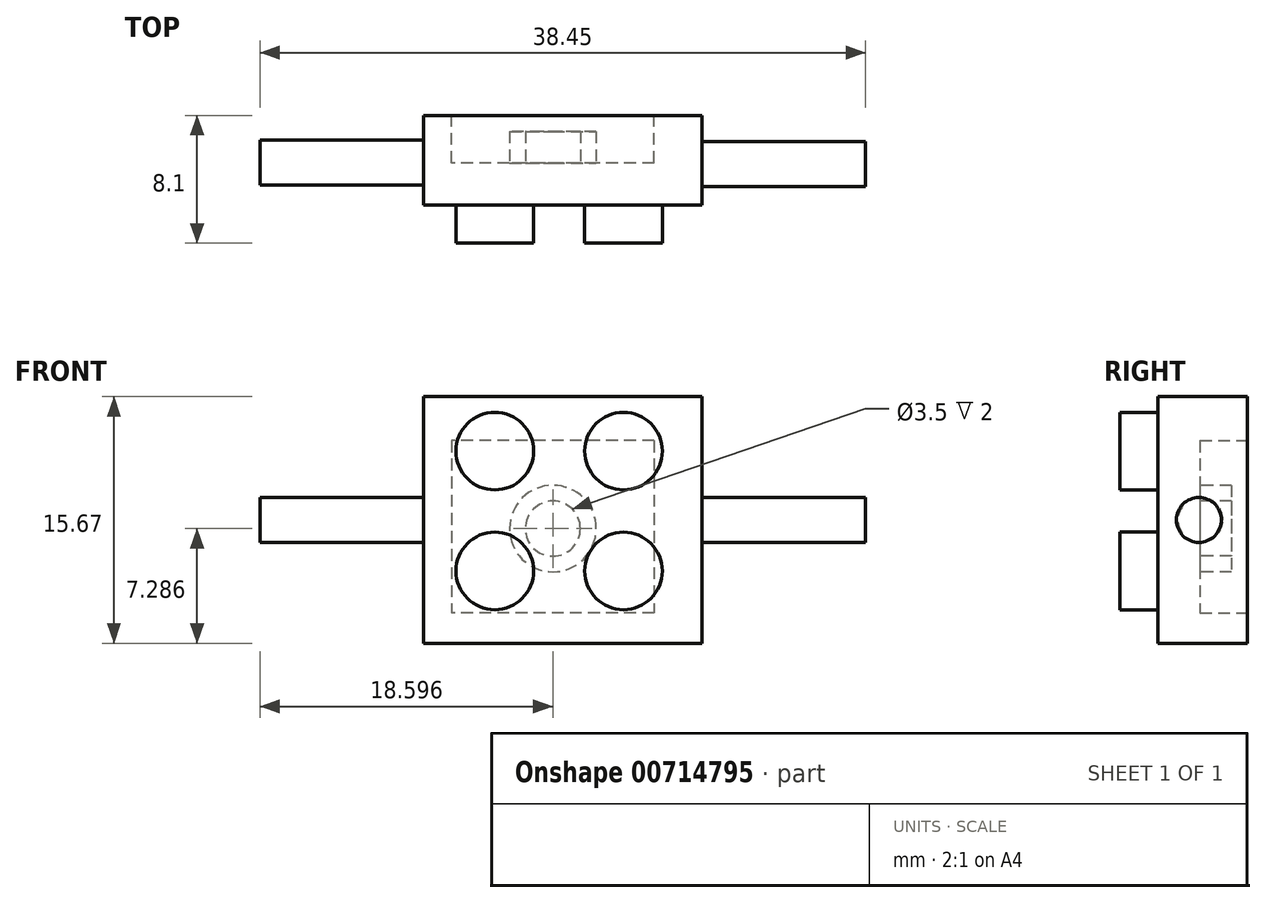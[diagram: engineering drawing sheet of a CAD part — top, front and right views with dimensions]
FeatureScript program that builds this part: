
annotation { "Feature Type Name" : "Feature", "Feature Type Description" : "" }
export const myFeature = defineFeature(function(context is Context, id is Id, definition is map)
    precondition{}
    {
        {
            var Q0;
            Q0=qCreatedBy(makeId("Front.planeOp"),FACE);
            var sketch = newSketch(context, id + "F0", { "sketchPlane" : qUnion([Q0])});
            skCircle(sketch, "E0", {"center": v(-31.02, 13.5) * mm, "radius": 7.84 * mm});
            skCircle(sketch, "E1", {"center": v(27.66, 13.5) * mm, "radius": 7.78 * mm});
            skCircle(sketch, "E2", {"center": v(-31.02, -35.79) * mm, "radius": 7.78 * mm});
            skCircle(sketch, "E3", {"center": v(27.66, -35.79) * mm, "radius": 7.78 * mm});
            skSolve(sketch);
        }
        {
            var Q0;
            Q0 = qSketchRegion(id + "F0", true);
            extrude(context, id + "F1", {"entities" : qUnion([Q0]), "depth" : 5.67 * mm, "offsetDistance" : 25 * mm});
        }
        {
            var Q0;
            Q0=qCreatedBy(makeId("Front.planeOp"),FACE);
            var sketch = newSketch(context, id + "F2", { "sketchPlane" : qUnion([Q0])});
            skLineSegment(sketch, "E4", {"start": v(-84.9, 44.94) * mm, "end": v(-67.21, 44.94) * mm});
            skLineSegment(sketch, "E5", {"start": v(-84.9, 29.27) * mm, "end": v(-67.21, 29.27) * mm});
            skPoint(sketch, "E6.start.orphan", {"position": v(-67.21, 39.5) * mm});
            skPoint(sketch, "E7.end.orphan", {"position": v(-84.9, 35.35) * mm});
            skLineSegment(sketch, "E8", {"start": v(-84.9, 44.94) * mm, "end": v(-84.9, 29.27) * mm});
            skLineSegment(sketch, "E9", {"start": v(-67.21, 44.94) * mm, "end": v(-67.21, 29.27) * mm});
            skSolve(sketch);
        }
        {
            var Q0;
            Q0 = qSketchRegion(id + "F2", true);
            extrude(context, id + "F3", {"entities" : qUnion([Q0]), "depth" : 5.67 * mm, "offsetDistance" : 25 * mm});
        }
        {
            var Q0;
            Q0=makeQuery(id+"F3.opExtrude","SWEPT_FACE",FACE,{"disambiguationData":[OSD([sQuery(id+"F2.wireOp",EDGE,"E8")])]});
            var sketch = newSketch(context, id + "F4", { "sketchPlane" : qUnion([Q0])});
            skPoint(sketch, "E10.centerSnap0", {"position": v(0, 37.1) * mm});
            skCircle(sketch, "E11", {"center": v(2.97, 37.1) * mm, "radius": 1.43 * mm});
            skSolve(sketch);
        }
        {
            var Q0;
            Q0 = qSketchRegion(id + "F4", true);
            extrude(context, id + "F5", {"entities" : qUnion([Q0]), "operationType" : NewBodyOperationType.ADD, "depth" : 10.38 * mm, "offsetDistance" : 25 * mm});
        }
        {
            var Q0;
            Q0=makeQuery(id+"F3.opExtrude","SWEPT_FACE",FACE,{"disambiguationData":[OSD([sQuery(id+"F2.wireOp",EDGE,"E9")])]});
            var sketch = newSketch(context, id + "F6", { "sketchPlane" : qUnion([Q0])});
            skCircle(sketch, "E12", {"center": v(-3.07, 37.1) * mm, "radius": 1.43 * mm});
            skPoint(sketch, "E12.centerSnap0", {"position": v(0, 37.1) * mm});
            skSolve(sketch);
        }
        {
            var Q0;
            Q0 = qSketchRegion(id + "F6", true);
            extrude(context, id + "F7", {"entities" : qUnion([Q0]), "operationType" : NewBodyOperationType.ADD, "depth" : 10.38 * mm, "offsetDistance" : 25 * mm});
        }
        {
            var Q0;
            Q0=makeQuery(id+"F3.opExtrude","CAP_FACE",FACE,{"disambiguationData":[OSD([sQuery(id+"F2.wireOp",EDGE,"E4"),sQuery(id+"F2.wireOp",EDGE,"E5"),sQuery(id+"F2.wireOp",EDGE,"E8"),sQuery(id+"F2.wireOp",EDGE,"E9")])],"isStart":false});
            var sketch = newSketch(context, id + "F8", { "sketchPlane" : qUnion([Q0])});
            skCircle(sketch, "E13", {"center": v(-80.37, 41.48) * mm, "radius": 2.46 * mm});
            skCircle(sketch, "E14", {"center": v(-72.2, 41.48) * mm, "radius": 2.46 * mm});
            skCircle(sketch, "E15", {"center": v(-72.2, 33.87) * mm, "radius": 2.46 * mm});
            skPoint(sketch, "E16.center.orphan", {"position": v(-80.37, 34.15) * mm});
            skCircle(sketch, "E17", {"center": v(-80.37, 33.87) * mm, "radius": 2.46 * mm});
            skSolve(sketch);
        }
        {
            var Q0;
            Q0 = qSketchRegion(id + "F8", true);
            extrude(context, id + "F9", {"entities" : qUnion([Q0]), "operationType" : NewBodyOperationType.ADD, "depth" : 2.42 * mm, "offsetDistance" : 25 * mm});
        }
        {
            var Q0;
            Q0=makeQuery(id+"F3.opExtrude","CAP_FACE",FACE,{"disambiguationData":[OSD([sQuery(id+"F2.wireOp",EDGE,"E4"),sQuery(id+"F2.wireOp",EDGE,"E5"),sQuery(id+"F2.wireOp",EDGE,"E8"),sQuery(id+"F2.wireOp",EDGE,"E9")])],"isStart":true});
            var sketch = newSketch(context, id + "F10", { "sketchPlane" : qUnion([Q0])});
            skLineSegment(sketch, "E18.bottom", {"start": v(70.25, 42.15) * mm, "end": v(83.12, 42.15) * mm});
            skLineSegment(sketch, "E18.top", {"start": v(70.25, 31.2) * mm, "end": v(83.12, 31.2) * mm});
            skLineSegment(sketch, "E18.left", {"start": v(70.25, 42.15) * mm, "end": v(70.25, 31.2) * mm});
            skLineSegment(sketch, "E18.right", {"start": v(83.12, 42.15) * mm, "end": v(83.12, 31.2) * mm});
            skSolve(sketch);
        }
        {
            var Q0;
            Q0 = qSketchRegion(id + "F10", true);
            extrude(context, id + "F11", {"entities" : qUnion([Q0]), "operationType" : NewBodyOperationType.REMOVE, "oppositeDirection" : true, "depth" : 3 * mm, "offsetDistance" : 25 * mm});
        }
        {
            var Q0;
            Q0=makeQuery(id+"F11.boolean.opBoolean","COPY",FACE,{"derivedFrom":makeQuery(id+"F11.opExtrude","CAP_FACE",FACE,{"disambiguationData":[OSD([sQuery(id+"F10.wireOp",EDGE,"E18.bottom"),sQuery(id+"F10.wireOp",EDGE,"E18.top"),sQuery(id+"F10.wireOp",EDGE,"E18.left"),sQuery(id+"F10.wireOp",EDGE,"E18.right")])],"isStart":false})});
            var sketch = newSketch(context, id + "F12", { "sketchPlane" : qUnion([Q0])});
            skCircle(sketch, "E19", {"center": v(76.68, 36.56) * mm, "radius": 2.75 * mm});
            skCircle(sketch, "E20", {"center": v(76.68, 36.56) * mm, "radius": 1.75 * mm});
            skSolve(sketch);
        }
        {
            var Q0;
            Q0 = qSketchRegion(id + "F12", true);
            extrude(context, id + "F13", {"entities" : qUnion([Q0]), "operationType" : NewBodyOperationType.ADD, "depth" : 2 * mm, "offsetDistance" : 25 * mm});
        }
        {
            var Q0;
            Q0=qCreatedBy(makeId("Front.planeOp"),FACE);
            var sketch = newSketch(context, id + "F14", { "sketchPlane" : qUnion([Q0])});
            skCircle(sketch, "E21", {"center": v(27.67, 13.74) * mm, "radius": 4.34 * mm});
            skCircle(sketch, "E22", {"center": v(-30.96, -35.55) * mm, "radius": 4.34 * mm});
            skCircle(sketch, "E23", {"center": v(27.96, -35.55) * mm, "radius": 4.34 * mm});
            skCircle(sketch, "E24", {"center": v(-31.25, 14.02) * mm, "radius": 4.34 * mm});
            skCircle(sketch, "E25", {"center": v(27.67, 13.74) * mm, "radius": 3.47 * mm});
            skCircle(sketch, "E26", {"center": v(-31.25, 14.02) * mm, "radius": 3.13 * mm});
            skCircle(sketch, "E27", {"center": v(27.96, -35.55) * mm, "radius": 4.29 * mm});
            skCircle(sketch, "E28", {"center": v(-30.96, -35.55) * mm, "radius": 4.1 * mm});
            skSolve(sketch);
        }
        {
            var Q0;
            Q0=makeQuery(id+"F14.imprint","IMPRINT",FACE,{"disambiguationData":[TD([[makeQuery(id+"F14.imprint","IMPRINT",EDGE,{"derivedFrom":sQuery(id+"F14.wireOp",EDGE,"E21")}),1.0]])]});
            var Q1;
            Q1=makeQuery(id+"F14.imprint","IMPRINT",FACE,{"disambiguationData":[TD([[makeQuery(id+"F14.imprint","IMPRINT",EDGE,{"derivedFrom":sQuery(id+"F14.wireOp",EDGE,"E24")}),1.0]])]});
            var Q2;
            Q2=makeQuery(id+"F14.imprint","IMPRINT",FACE,{"disambiguationData":[TD([[makeQuery(id+"F14.imprint","IMPRINT",EDGE,{"derivedFrom":sQuery(id+"F14.wireOp",EDGE,"E22")}),1.0]])]});
            var Q3;
            Q3=makeQuery(id+"F14.imprint","IMPRINT",FACE,{"disambiguationData":[TD([[makeQuery(id+"F14.imprint","IMPRINT",EDGE,{"derivedFrom":sQuery(id+"F14.wireOp",EDGE,"E23")}),1.0]])]});
            extrude(context, id + "F15", {"entities" : qUnion([Q0, Q1, Q2, Q3]), "operationType" : NewBodyOperationType.ADD, "depth" : 25 * mm, "offsetDistance" : 25 * mm});
        }
        {
            var Q0;
            Q0 = qSketchRegion(id + "F14", true);
            extrude(context, id + "F16", {"entities" : qUnion([Q0]), "operationType" : NewBodyOperationType.REMOVE, "oppositeDirection" : true, "depth" : 25 * mm, "offsetDistance" : 25 * mm});
        }
        {
            var Q0;
            Q0=makeQuery(id+"F1.opExtrude","SWEPT_BODY",BODY,{"disambiguationData":[OSD([sQuery(id+"F0.wireOp",EDGE,"E1")])]});
            var Q1;
            Q1=makeQuery(id+"F1.opExtrude","SWEPT_BODY",BODY,{"disambiguationData":[OSD([sQuery(id+"F0.wireOp",EDGE,"E0")])]});
            var Q2;
            Q2=makeQuery(id+"F1.opExtrude","SWEPT_BODY",BODY,{"disambiguationData":[OSD([sQuery(id+"F0.wireOp",EDGE,"E2")])]});
            var Q3;
            Q3=makeQuery(id+"F1.opExtrude","SWEPT_BODY",BODY,{"disambiguationData":[OSD([sQuery(id+"F0.wireOp",EDGE,"E3")])]});
            deleteBodies(context, id + "F17", {"entities" : qUnion([Q0, Q1, Q2, Q3])});
        }
    });
